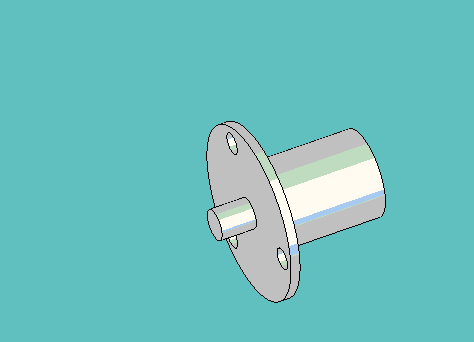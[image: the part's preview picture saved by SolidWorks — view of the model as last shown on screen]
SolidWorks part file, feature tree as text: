
SOLIDWORKS PART (.sldprt)
format: sldprt  version: not decoded by parser v0  size: 168,448 bytes
history: native  units: mm
features: sketch x3, extrude x3, material x1 (+11 scaffold rows collapsed)
feature tree (18):
  scaffold x11  (default folders/planes/origin — collapsed)
  material  "Material <not specified>"
  sketch  "Sketch1"  dims[c1.D1=44.0mm c1.D4=35.0mm c1.D5=5.5mm c1.D6=5.5mm c1.D7=5.5mm c1.D2=~42.815038mm c2.D2=120.0deg c2.D3=~42.815038mm c3.D3=120.0deg]
  extrude  "Extrude1"  Depth=2.4mm
  sketch  "Sketch2"  dims[D1=7.8mm]
  extrude  "Extrude2"  Depth=9mm
  sketch  "Sketch3"  dims[D1=22.0mm]
  extrude  "Extrude3"  Depth=28mm
decode coverage: 6 of 6 modeling features carry decoded parameters
note: ~ marks probable driven/reference dimensions
note: suppression state not decoded; provenance and decode notes live in map.json
